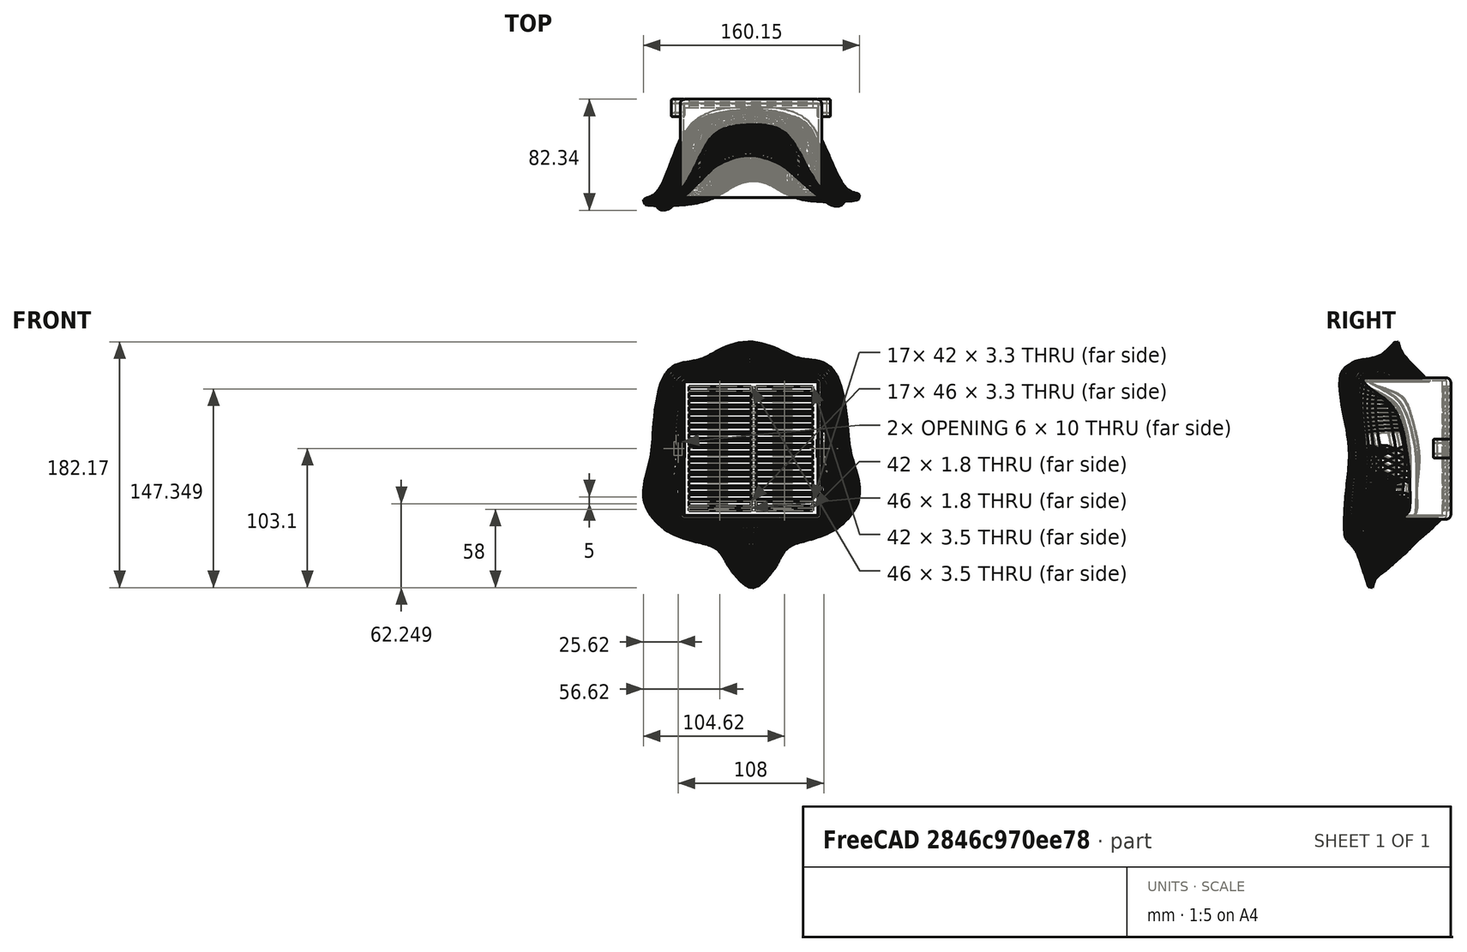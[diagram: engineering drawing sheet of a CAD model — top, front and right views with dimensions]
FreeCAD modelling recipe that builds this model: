
FCSTD DOCUMENT  (FreeCAD 0.17R13541 (Git))
Label: facemask_combined
License: All rights reserved
LicenseURL: http://en.wikipedia.org/wiki/All_rights_reserved
objects: Part::Box×31, Part::Cut×7, Part::Feature×5, Part::MultiFuse×4, Part::Fillet×3, Mesh::Feature×2
note: 50 computed .brp shape members not serialized (recipe doc carries the construction recipe); baked Part::Feature solids carry a one-line shape summary decoded from their .brp

FEATURE [Part::Box] Box  label="Cube"
  AttacherType = Attacher::AttachEngine3D
  Height = 70
  Length = 104.8
  Placement = pos=(-52.4,-52.4,0) rot=(0,0,1;0rad)
  Width = 104.8
FEATURE [Part::Box] Box001  label="Cube001"
  AttacherType = Attacher::AttachEngine3D
  Height = 70
  Length = 100
  Placement = pos=(-50,-50,3.2) rot=(0,0,1;0rad)
  Width = 100
FEATURE [Part::Box] Box002  label="Cube002"
  AttacherType = Attacher::AttachEngine3D
  Height = 80
  Length = 92
  Placement = pos=(-46,-46,-5) rot=(0,0,1;0rad)
  Width = 92
FEATURE [Part::Box] Box003  label="fin"
  AttacherType = Attacher::AttachEngine3D
  Height = 7
  Length = 104
  Placement = pos=(-52,0,-1) rot=(1,0,0;0.785398rad)
  Width = 1.2
FEATURE [Part::Cut] Cut
  Base = -> Box
  Tool = -> Box002
FEATURE [Part::Box] Box004  label="fin001"
  AttacherType = Attacher::AttachEngine3D
  Height = 7
  Length = 104
  Placement = pos=(-52,5,-1) rot=(1,0,0;0.785398rad)
  Width = 1.2
FEATURE [Part::Box] Box005  label="fin002"
  AttacherType = Attacher::AttachEngine3D
  Height = 7
  Length = 104
  Placement = pos=(-52,15,-1) rot=(1,0,0;0.785398rad)
  Width = 1.2
FEATURE [Part::Box] Box006  label="fin003"
  AttacherType = Attacher::AttachEngine3D
  Height = 7
  Length = 104
  Placement = pos=(-52,10,-1) rot=(1,0,0;0.785398rad)
  Width = 1.2
FEATURE [Part::Box] Box007  label="fin004"
  AttacherType = Attacher::AttachEngine3D
  Height = 7
  Length = 104
  Placement = pos=(-52,15,-1) rot=(1,0,0;0.785398rad)
  Width = 1.2
FEATURE [Part::Box] Box008  label="fin005"
  AttacherType = Attacher::AttachEngine3D
  Height = 7
  Length = 104
  Placement = pos=(-52,20,-1) rot=(1,0,0;0.785398rad)
  Width = 1.2
FEATURE [Part::Box] Box009  label="fin006"
  AttacherType = Attacher::AttachEngine3D
  Height = 7
  Length = 104
  Placement = pos=(-52,25,-1) rot=(1,0,0;0.785398rad)
  Width = 1.2
FEATURE [Part::Box] Box010  label="fin007"
  AttacherType = Attacher::AttachEngine3D
  Height = 7
  Length = 104
  Placement = pos=(-52,30,-1) rot=(1,0,0;0.785398rad)
  Width = 1.2
FEATURE [Part::Box] Box011  label="fin008"
  AttacherType = Attacher::AttachEngine3D
  Height = 7
  Length = 104
  Placement = pos=(-52,35,-1) rot=(1,0,0;0.785398rad)
  Width = 1.2
FEATURE [Part::Box] Box012  label="fin009"
  AttacherType = Attacher::AttachEngine3D
  Height = 7
  Length = 104
  Placement = pos=(-52,40,-1) rot=(1,0,0;0.785398rad)
  Width = 1.2
FEATURE [Part::Box] Box013  label="fin010"
  AttacherType = Attacher::AttachEngine3D
  Height = 7
  Length = 104
  Placement = pos=(-52,45,-1) rot=(1,0,0;0.785398rad)
  Width = 1.2
FEATURE [Part::Box] Box014  label="fint1"
  AttacherType = Attacher::AttachEngine3D
  Height = 7
  Length = 104
  Placement = pos=(-52,-45,-1) rot=(1,0,0;0.785398rad)
  Width = 1.2
FEATURE [Part::Box] Box015  label="fint002"
  AttacherType = Attacher::AttachEngine3D
  Height = 7
  Length = 104
  Placement = pos=(-52,-40,-1) rot=(1,0,0;0.785398rad)
  Width = 1.2
FEATURE [Part::Box] Box016  label="fint003"
  AttacherType = Attacher::AttachEngine3D
  Height = 7
  Length = 104
  Placement = pos=(-52,-35,-1) rot=(1,0,0;0.785398rad)
  Width = 1.2
FEATURE [Part::Box] Box017  label="fint004"
  AttacherType = Attacher::AttachEngine3D
  Height = 7
  Length = 104
  Placement = pos=(-52,-30,-1) rot=(1,0,0;0.785398rad)
  Width = 1.2
FEATURE [Part::Box] Box018  label="fint005"
  AttacherType = Attacher::AttachEngine3D
  Height = 7
  Length = 104
  Placement = pos=(-52,-20,-1) rot=(1,0,0;0.785398rad)
  Width = 1.2
FEATURE [Part::Box] Box019  label="fint006"
  AttacherType = Attacher::AttachEngine3D
  Height = 7
  Length = 104
  Placement = pos=(-52,-25,-1) rot=(1,0,0;0.785398rad)
  Width = 1.2
FEATURE [Part::Box] Box020  label="fint007"
  AttacherType = Attacher::AttachEngine3D
  Height = 7
  Length = 104
  Placement = pos=(-52,-20,-1) rot=(1,0,0;0.785398rad)
  Width = 1.2
FEATURE [Part::Box] Box021  label="fint008"
  AttacherType = Attacher::AttachEngine3D
  Height = 7
  Length = 104
  Placement = pos=(-52,-15,-1) rot=(1,0,0;0.785398rad)
  Width = 1.2
FEATURE [Part::Box] Box022  label="fint009"
  AttacherType = Attacher::AttachEngine3D
  Height = 7
  Length = 104
  Placement = pos=(-52,-10,-1) rot=(1,0,0;0.785398rad)
  Width = 1.2
FEATURE [Part::Box] Box023  label="fint010"
  AttacherType = Attacher::AttachEngine3D
  Height = 7
  Length = 104
  Placement = pos=(-52,-5,-1) rot=(1,0,0;0.785398rad)
  Width = 1.2
FEATURE [Part::MultiFuse] Fusion  label="fins"
  Shapes = -> [Box003,Box004,Box016,Box015,Box008,Box006,Box009,Box010,Box012,Box013,Box007,Box014,Box011,Box005,Box019,Box022,Box023,Box017,Box021,Box020,Box018]
FEATURE [Part::Box] Box024  label="Cube003"
  AttacherType = Attacher::AttachEngine3D
  Height = 10
  Length = 4
  Placement = pos=(0,-52,2) rot=(0,0,1;0rad)
  Width = 104
FEATURE [Part::MultiFuse] Fusion001
  Shapes = -> [Cut,Fusion,Box024]
FEATURE [Part::Cut] Cut001
  Base = -> Fusion001
  Tool = -> Box001
FEATURE [Part::Box] Box025  label="Cube004"
  AttacherType = Attacher::AttachEngine3D
  Height = 10
  Length = 120
  Placement = pos=(-60,-60,-10) rot=(0,0,1;0rad)
  Width = 120
FEATURE [Part::Cut] Cut002
  Base = -> Cut001
  Tool = -> Box025
FEATURE [Part::Fillet] Fillet
  Base = -> Cut002
  Edges = 12 edges: [Edge1 r=3.5,Edge3 r=3.5,Edge4 r=3.5,Edge5 r=3.5,Edge6 r=3.5,Edge14 r=3.5,Edge15 r=3.5,Edge170 r=3.5,Edge171 r=1,Edge172 r=1,Edge174 r=1,Edge176 r=1]
FEATURE [Part::Box] Box026  label="Cube005"
  AttacherType = Attacher::AttachEngine3D
  Height = 10
  Length = 10
  Placement = pos=(49,-7,0) rot=(0,0,1;0rad)
  Width = 14
FEATURE [Part::Box] Box027  label="Cube006"
  AttacherType = Attacher::AttachEngine3D
  Height = 14
  Length = 4
  Placement = pos=(52,-4,-1) rot=(0,0,1;0rad)
  Width = 8
FEATURE [Part::Cut] Cut003
  Base = -> Box026
  Tool = -> Box027
FEATURE [Part::Box] Box028  label="Cube007"
  AttacherType = Attacher::AttachEngine3D
  Height = 10
  Length = 10
  Placement = pos=(49,-7,0) rot=(0,0,1;0rad)
  Width = 14
FEATURE [Part::Box] Box029  label="Cube008"
  AttacherType = Attacher::AttachEngine3D
  Height = 14
  Length = 4
  Placement = pos=(52,-4,-1) rot=(0,0,1;0rad)
  Width = 8
FEATURE [Part::Cut] Cut004
  Base = -> Box028
  Placement = pos=(-108,0,0) rot=(0,0,1;0rad)
  Tool = -> Box029
FEATURE [Part::Fillet] Fillet001
  Base = -> Cut004
  Edges = 24 edges r=1: [Edge1,Edge2,Edge3,Edge4,Edge5,Edge6,Edge7,Edge8,Edge9,Edge10,Edge11,Edge12,Edge13,Edge14,Edge15,Edge16,Edge17,Edge18,Edge19,Edge20,Edge21,Edge22,Edge23,Edge24]
FEATURE [Part::Fillet] Fillet002
  Base = -> Cut003
  Edges = 24 edges r=1: [Edge1,Edge2,Edge3,Edge4,Edge5,Edge6,Edge7,Edge8,Edge9,Edge10,Edge11,Edge12,Edge13,Edge14,Edge15,Edge16,Edge17,Edge18,Edge19,Edge20,Edge21,Edge22,Edge23,Edge24]
FEATURE [Part::MultiFuse] Fusion002
  Placement = pos=(0,0,0) rot=(1,0,0;1.5708rad)
  Shapes = -> [Fillet,Fillet001,Fillet002]
FEATURE [Mesh::Feature] cup_cutbody
  Placement = pos=(0,0,0) rot=(0,1,0;3.14159rad)
FEATURE [Part::Feature] cup_cutbody001
  shape: bbox 158.5 x 392 x 181.1 mm, 20160 faces, 0 solids (baked)
FEATURE [Part::Feature] Fusion002_solid  label="Fusion002 (Solid)"
  shape: bbox 118 x 70 x 104.8 mm, 397 faces (baked)
FEATURE [Part::Feature] cup_cutbody001_solid  label="cup_cutbody001 (Solid)"
  shape: bbox 158.5 x 392 x 181.1 mm, 20160 faces (baked)
FEATURE [Part::Cut] Cut005
  Base = -> Fusion002_solid
  Placement = pos=(0,3,0) rot=(0,0,1;0rad)
  Tool = -> cup_cutbody001_solid
FEATURE [Mesh::Feature] cup
  Placement = pos=(0,0,0) rot=(0,1,0;3.14159rad)
FEATURE [Part::Feature] cup001
  shape: bbox 160.2 x 77.63 x 182.2 mm, 20160 faces, 0 solids (baked)
FEATURE [Part::Feature] cup001_solid  label="cup001 (Solid)"
  shape: bbox 160.2 x 77.63 x 182.2 mm, 20160 faces (baked)
FEATURE [Part::MultiFuse] Fusion003
  Shapes = -> [cup001_solid,Cut005]
FEATURE [Part::Box] Box030  label="Cube009"
  AttacherType = Attacher::AttachEngine3D
  Height = 99
  Length = 99
  Placement = pos=(-49.5,-100,-49.5) rot=(0,0,1;0rad)
  Width = 99
FEATURE [Part::Cut] Cut006  label="facemask"
  Base = -> Fusion003
  Tool = -> Box030
